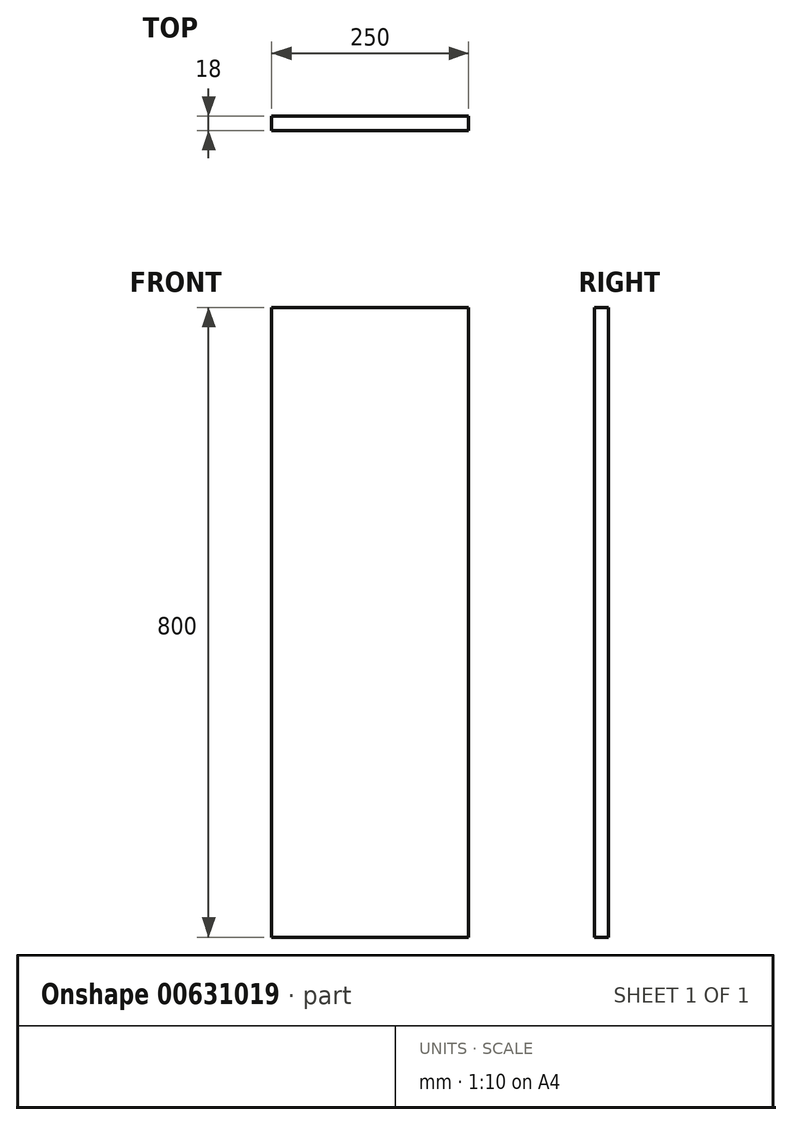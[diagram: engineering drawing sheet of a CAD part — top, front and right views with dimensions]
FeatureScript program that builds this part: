
annotation { "Feature Type Name" : "Feature", "Feature Type Description" : "" }
export const myFeature = defineFeature(function(context is Context, id is Id, definition is map)
    precondition{}
    {
        {
            var Q0;
            Q0=qCreatedBy(makeId("Front.planeOp"),FACE);
            var sketch = newSketch(context, id + "F0", { "sketchPlane" : qUnion([Q0])});
            skLineSegment(sketch, "E0.bottom", {"start": v(0, 0) * mm, "end": v(-250, 0) * mm});
            skLineSegment(sketch, "E0.top", {"start": v(0, -800) * mm, "end": v(-250, -800) * mm});
            skLineSegment(sketch, "E0.left", {"start": v(0, 0) * mm, "end": v(0, -800) * mm});
            skLineSegment(sketch, "E0.right", {"start": v(-250, 0) * mm, "end": v(-250, -800) * mm});
            skSolve(sketch);
        }
        {
            var Q0;
            Q0 = qSketchRegion(id + "F0", true);
            extrude(context, id + "F1", {"entities" : qUnion([Q0]), "depth" : 18 * mm, "offsetDistance" : 25 * mm});
        }
    });
